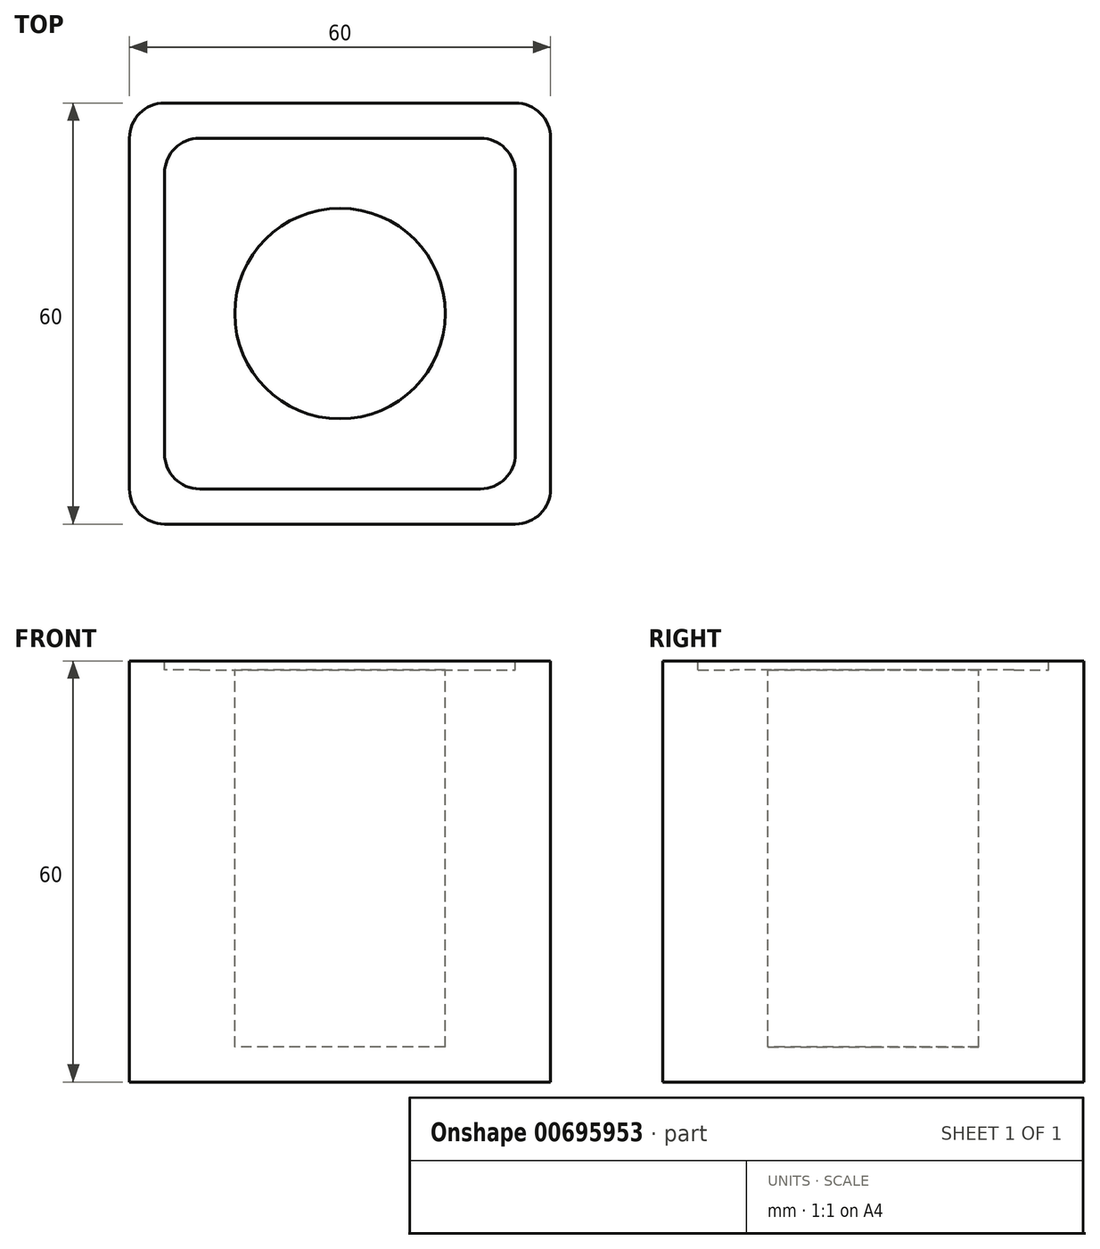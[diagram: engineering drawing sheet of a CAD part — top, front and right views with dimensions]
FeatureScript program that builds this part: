
annotation { "Feature Type Name" : "Feature", "Feature Type Description" : "" }
export const myFeature = defineFeature(function(context is Context, id is Id, definition is map)
    precondition{}
    {
        {
            var Q0;
            Q0=qCreatedBy(makeId("Top.planeOp"),FACE);
            var sketch = newSketch(context, id + "F0", { "sketchPlane" : qUnion([Q0])});
            skLineSegment(sketch, "E0.bottom", {"start": v(-25, 30) * mm, "end": v(25, 30) * mm});
            skLineSegment(sketch, "E0.top", {"start": v(-25, -30) * mm, "end": v(25, -30) * mm});
            skLineSegment(sketch, "E0.left", {"start": v(-30, 25) * mm, "end": v(-30, -25) * mm});
            skLineSegment(sketch, "E0.right", {"start": v(30, 25) * mm, "end": v(30, -25) * mm});
            skPoint(sketch, "E0.middle", {"position": v(0, 0) * mm});
            skPoint(sketch, "E1.visualSharp", {"position": v(-30, 30) * mm});
            skArc(sketch, "E1.filletArc", {"start": v(-25, 30) * mm, "mid": v(-28.54, 28.54) * mm, "end": v(-30, 25) * mm});
            skPoint(sketch, "E2.visualSharp", {"position": v(30, 30) * mm});
            skArc(sketch, "E2.filletArc", {"start": v(30, 25) * mm, "mid": v(28.54, 28.54) * mm, "end": v(25, 30) * mm});
            skPoint(sketch, "E3.visualSharp", {"position": v(-30, -30) * mm});
            skArc(sketch, "E3.filletArc", {"start": v(-30, -25) * mm, "mid": v(-28.54, -28.54) * mm, "end": v(-25, -30) * mm});
            skPoint(sketch, "E4.visualSharp", {"position": v(30, -30) * mm});
            skArc(sketch, "E4.filletArc", {"start": v(25, -30) * mm, "mid": v(28.54, -28.54) * mm, "end": v(30, -25) * mm});
            skSolve(sketch);
        }
        {
            var Q0;
            Q0=makeQuery(id+"F0.imprint","IMPRINT",FACE,{"disambiguationData":[TD([[makeQuery(id+"F0.imprint","IMPRINT",EDGE,{"derivedFrom":sQuery(id+"F0.wireOp",EDGE,"E0.bottom")}),-1.0]])]});
            extrude(context, id + "F1", {"entities" : qUnion([Q0]), "depth" : 60 * mm, "offsetDistance" : 25 * mm});
        }
        {
            var Q0;
            Q0=makeQuery(id+"F1.opExtrude","CAP_FACE",FACE,{"disambiguationData":[OSD([sQuery(id+"F0.wireOp",EDGE,"E0.bottom"),sQuery(id+"F0.wireOp",EDGE,"E0.top"),sQuery(id+"F0.wireOp",EDGE,"E0.left"),sQuery(id+"F0.wireOp",EDGE,"E0.right"),sQuery(id+"F0.wireOp",EDGE,"E1.filletArc"),sQuery(id+"F0.wireOp",EDGE,"E2.filletArc"),sQuery(id+"F0.wireOp",EDGE,"E3.filletArc"),sQuery(id+"F0.wireOp",EDGE,"E4.filletArc")])],"isStart":false});
            var sketch = newSketch(context, id + "F2", { "sketchPlane" : qUnion([Q0])});
            skLineSegment(sketch, "E5.bottom", {"start": v(-20, 25) * mm, "end": v(20, 25) * mm});
            skLineSegment(sketch, "E5.top", {"start": v(-20, -25) * mm, "end": v(20, -25) * mm});
            skLineSegment(sketch, "E5.left", {"start": v(-25, 20) * mm, "end": v(-25, -20) * mm});
            skLineSegment(sketch, "E5.right", {"start": v(25, 20) * mm, "end": v(25, -20) * mm});
            skPoint(sketch, "E5.middle", {"position": v(0, 0) * mm});
            skPoint(sketch, "E6.visualSharp", {"position": v(25, 25) * mm});
            skArc(sketch, "E6.filletArc", {"start": v(25, 20) * mm, "mid": v(23.54, 23.54) * mm, "end": v(20, 25) * mm});
            skPoint(sketch, "E7.visualSharp", {"position": v(25, -25) * mm});
            skArc(sketch, "E7.filletArc", {"start": v(20, -25) * mm, "mid": v(23.54, -23.54) * mm, "end": v(25, -20) * mm});
            skPoint(sketch, "E8.visualSharp", {"position": v(-25, -25) * mm});
            skArc(sketch, "E8.filletArc", {"start": v(-25, -20) * mm, "mid": v(-23.54, -23.54) * mm, "end": v(-20, -25) * mm});
            skPoint(sketch, "E9.visualSharp", {"position": v(-25, 25) * mm});
            skArc(sketch, "E9.filletArc", {"start": v(-20, 25) * mm, "mid": v(-23.54, 23.54) * mm, "end": v(-25, 20) * mm});
            skCircle(sketch, "E10", {"center": v(0, 0) * mm, "radius": 15 * mm});
            skSolve(sketch);
        }
        {
            var Q0;
            Q0=makeQuery(id+"F2.imprint","IMPRINT",FACE,{"disambiguationData":[TD([[makeQuery(id+"F2.imprint","IMPRINT",EDGE,{"derivedFrom":sQuery(id+"F2.wireOp",EDGE,"E5.bottom")}),-1.0]])]});
            extrude(context, id + "F3", {"entities" : qUnion([Q0]), "operationType" : NewBodyOperationType.REMOVE, "oppositeDirection" : true, "depth" : 1.3 * mm, "offsetDistance" : 25 * mm});
        }
        {
            var Q0;
            Q0=makeQuery(id+"F3.boolean.opBoolean","SPLIT",FACE,{"disambiguationData":[TD([makeQuery(id+"F3.opExtrude","SWEPT_FACE",FACE,{"disambiguationData":[OSD([sQuery(id+"F2.wireOp",EDGE,"E10")])]})])],"derivedFrom":makeQuery(id+"F1.opExtrude","CAP_FACE",FACE,{"disambiguationData":[OSD([sQuery(id+"F0.wireOp",EDGE,"E0.bottom"),sQuery(id+"F0.wireOp",EDGE,"E0.top"),sQuery(id+"F0.wireOp",EDGE,"E0.left"),sQuery(id+"F0.wireOp",EDGE,"E0.right"),sQuery(id+"F0.wireOp",EDGE,"E1.filletArc"),sQuery(id+"F0.wireOp",EDGE,"E2.filletArc"),sQuery(id+"F0.wireOp",EDGE,"E3.filletArc"),sQuery(id+"F0.wireOp",EDGE,"E4.filletArc")])],"isStart":false})});
            extrude(context, id + "F4", {"entities" : qUnion([Q0]), "operationType" : NewBodyOperationType.REMOVE, "oppositeDirection" : true, "depth" : 55 * mm, "offsetDistance" : 25 * mm});
        }
    });
